# Revit family: QF_Varimixer_ERGO140
name_source: partatom
category: Specialty Equipment
units: mm (PartAtom-declared; Revit-internal decimal feet)

## family parameters
Always vertical = Yes
Cut with Voids When Loaded = No
OmniClass Number = 23.40.40.14.14.11
OmniClass Title = Food Mixers
Part Type = Normal
Room Calculation Point = No
Round Connector Dimension = Use Diameter
Shared = No
Work Plane-Based = No

## types (3) — shared parameters
Bowl size = 140 liter
Depth = 1300.5 mm
Description = Planetary mixer ERGO140
Electrical connection height = 1910.3 mm
Height = 2057.4 mm
Homepage = https://varimixer.com
Ingress protection = IP53 (option IP54)
Length = 1661.2 mm
Manufacturer = Varimixer A/S
Model = ERGO140
Panel name = VL-4
Plug included = No
Product description = Planetary mixer, heavy duty for whipping, kneading and mixing. 
Ergonomic - no heavy lifting
Product name = AR30
URL = www.varimixer.com
URL datasheet = https://varimixer.com
Weight in Pounds = 1124
Weight in kilograms = 525

## per-type parameters (varying)
| type | Connected with neutral | Cycle | Full load current | Horsepower | Number of phases | Power | Voltage |
| 400V/50Hz/3Ph/Europe | Yes | 50 Hz | 11 A |  | 3 | 5500 W | 400 V |
| 480V/60Hz/3Ph/USA | Yes | 60 Hz | 16 A | 7 hp | 3 | 5500 W | 480 V |
| Others on Request | No | 0 Hz | 0 A |  | 0 | 0 W | 0 V |

## geometry (parser evidence)
native form markers: Blend x4, Sweep x2
no freeform markers — native parametric forms only
